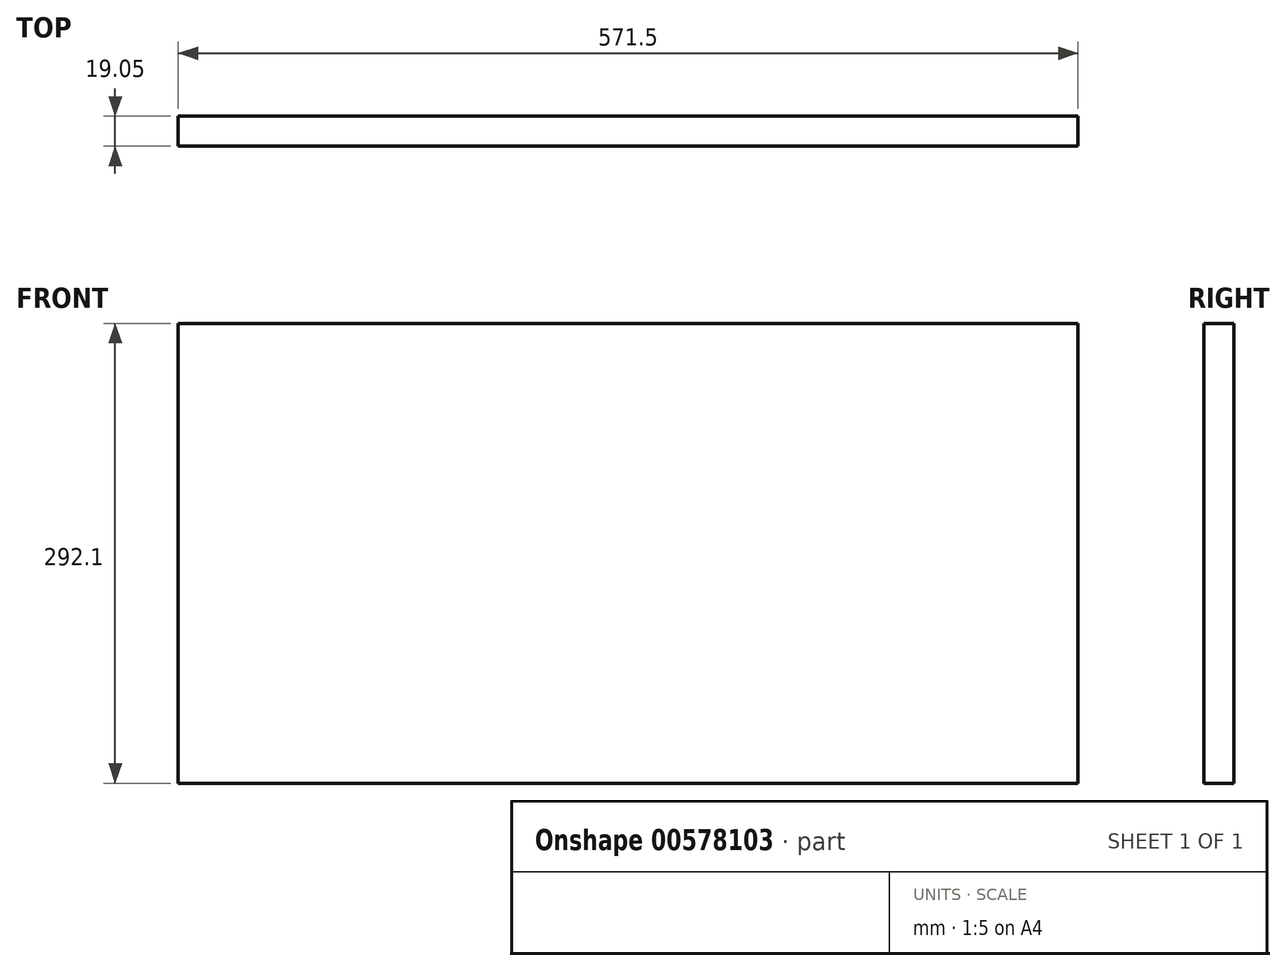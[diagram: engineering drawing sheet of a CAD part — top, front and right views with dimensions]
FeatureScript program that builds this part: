
annotation { "Feature Type Name" : "Feature", "Feature Type Description" : "" }
export const myFeature = defineFeature(function(context is Context, id is Id, definition is map)
    precondition{}
    {
        {
            var Q0;
            Q0=qCreatedBy(makeId("Front.planeOp"),FACE);
            var sketch = newSketch(context, id + "F0", { "sketchPlane" : qUnion([Q0])});
            skLineSegment(sketch, "E0.bottom", {"start": v(0, 0) * mm, "end": v(571.5, 0) * mm});
            skLineSegment(sketch, "E0.top", {"start": v(0, 292.1) * mm, "end": v(571.5, 292.1) * mm});
            skLineSegment(sketch, "E0.left", {"start": v(0, 0) * mm, "end": v(0, 292.1) * mm});
            skLineSegment(sketch, "E0.right", {"start": v(571.5, 0) * mm, "end": v(571.5, 292.1) * mm});
            skSolve(sketch);
        }
        {
            var Q0;
            Q0 = qSketchRegion(id + "F0", true);
            extrude(context, id + "F1", {"entities" : qUnion([Q0]), "depth" : 19.05 * mm, "offsetDistance" : 25.4 * mm});
        }
    });
